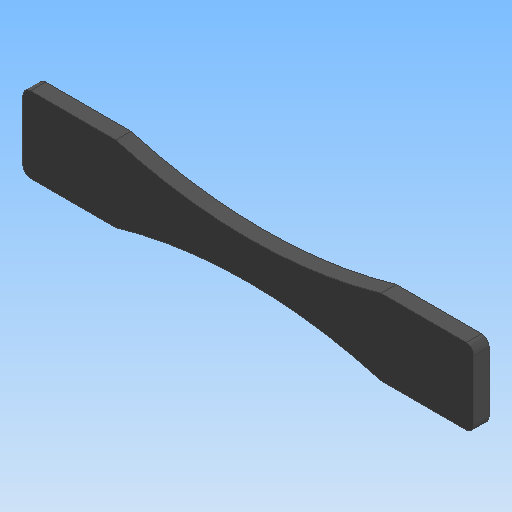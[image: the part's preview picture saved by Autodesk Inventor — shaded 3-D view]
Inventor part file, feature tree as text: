
AUTODESK INVENTOR PART (.ipt)
format: ipt  version: 2020 (Build 240168000, 168)  size: 121,856 bytes
history: native  units: mm
features: other x1, extrude x1
ambient origin geometry x8: Origin, YZ Plane, XZ Plane, XY Plane, X Axis, Y Axis, Z Axis, Center Point
bodies: Body1 (feature_tree)
feature tree (2):
  other  "實體1"
  extrude  "擠出1"  Depth=59.5mm
